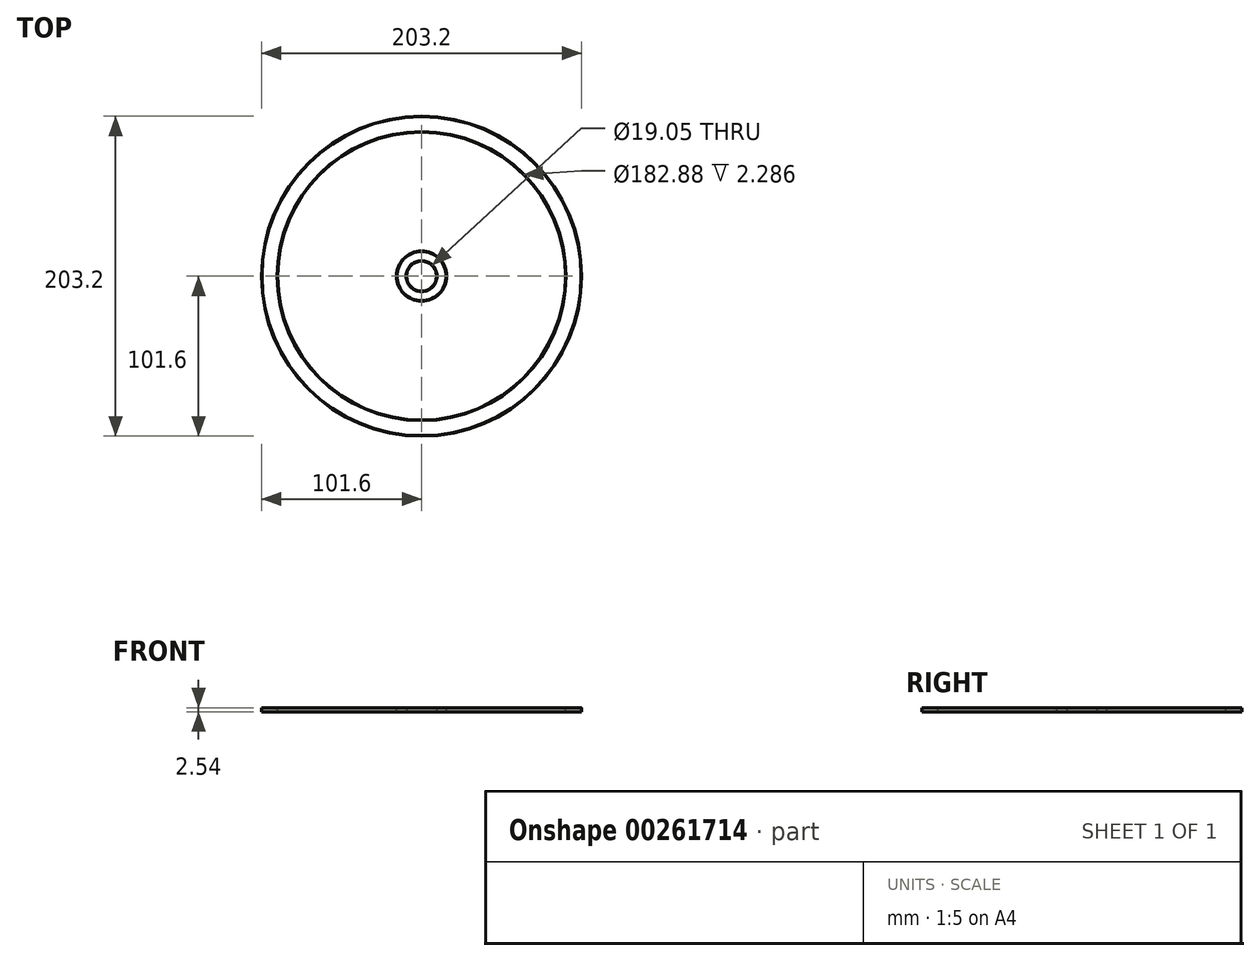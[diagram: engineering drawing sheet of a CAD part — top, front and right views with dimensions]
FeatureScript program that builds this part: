
annotation { "Feature Type Name" : "Feature", "Feature Type Description" : "" }
export const myFeature = defineFeature(function(context is Context, id is Id, definition is map)
    precondition{}
    {
        {
            var Q0;
            Q0=qCreatedBy(makeId("Top.planeOp"),FACE);
            var sketch = newSketch(context, id + "F0", { "sketchPlane" : qUnion([Q0])});
            skCircle(sketch, "E0", {"center": v(0, 0) * mm, "radius": 101.6 * mm});
            skSolve(sketch);
        }
        {
            var Q0;
            Q0=qSketchRegion(id+"F0",true);
            extrude(context, id + "F1", {"entities" : qUnion([Q0]), "depth" : 2.54 * mm});
        }
        {
            var Q0;
            Q0=makeQuery(id+"F1.opExtrude","CAP_FACE",FACE,{"disambiguationData":[OSD([sQuery(id+"F0.wireOp",EDGE,"E0")])],"isStart":true});
            var sketch = newSketch(context, id + "F2", { "sketchPlane" : qUnion([Q0])});
            skCircle(sketch, "E1", {"center": v(0, 0) * mm, "radius": 9.53 * mm});
            skSolve(sketch);
        }
        {
            var Q0;
            Q0=qSketchRegion(id+"F2",true);
            extrude(context, id + "F3", {"entities" : qUnion([Q0]), "operationType" : NewBodyOperationType.REMOVE, "oppositeDirection" : true, "depth" : 25.4 * mm});
        }
        {
            var Q0;
            Q0=makeQuery(id+"F1.opExtrude","CAP_FACE",FACE,{"disambiguationData":[OSD([sQuery(id+"F0.wireOp",EDGE,"E0")])],"isStart":false});
            var sketch = newSketch(context, id + "F4", { "sketchPlane" : qUnion([Q0])});
            skCircle(sketch, "E2", {"center": v(0, 0) * mm, "radius": 15.88 * mm});
            skCircle(sketch, "E3", {"center": v(0, 0) * mm, "radius": 91.44 * mm});
            skSolve(sketch);
        }
        {
            var Q0;
            Q0=qSketchRegion(id+"F4",true);
            extrude(context, id + "F5", {"entities" : qUnion([Q0]), "operationType" : NewBodyOperationType.REMOVE, "endBound" : BoundingType.THROUGH_ALL, "oppositeDirection" : true, "depth" : 25.4 * mm});
        }
        {
            var Q0;
            {var subQ0=sQuery(id+"F0.wireOp",EDGE,"E0");var subQ1=makeQuery(id+"F1.opExtrude","CAP_FACE",FACE,{"disambiguationData":[OSD([subQ0])],"isStart":false});Q0=makeQuery(id+"FSbwxRyUAKNEHpr_1.boolean.opBoolean","MERGE",FACE,{"derivedFrom":[makeQuery(id+"F5.boolean.opBoolean","SPLIT",FACE,{"disambiguationData":[TD([makeQuery(id+"F1.opExtrude","SWEPT_FACE",FACE,{"disambiguationData":[OSD([subQ0])]})])],"derivedFrom":subQ1}),makeQuery(id+"F5.boolean.opBoolean","SPLIT",FACE,{"disambiguationData":[TD([makeQuery(id+"F3.boolean.opBoolean","COPY",FACE,{"derivedFrom":makeQuery(id+"F3.opExtrude","SWEPT_FACE",FACE,{"disambiguationData":[OSD([sQuery(id+"F2.wireOp",EDGE,"E1")])]})})])],"derivedFrom":subQ1}),makeQuery(id+"FSbwxRyUAKNEHpr_1.opExtrude","CAP_FACE",FACE,{"disambiguationData":[OSD([sQuery(id+"FxIeaUR3CMKQrPm_1.wireOp",EDGE,"QbkZTcdc-0FBD-zTaQ-hJOD-ObugmLj84BvM"),sQuery(id+"FxIeaUR3CMKQrPm_1.wireOp",EDGE,"wRuti5NG-CyyP-u1Pt-0mSH-9gk4yfvUaacR"),sQuery(id+"FxIeaUR3CMKQrPm_1.wireOp",EDGE,"1yoEojWW-aKa5-Gd0I-27Oc-1dL5FRi6qJQZ"),sQuery(id+"FxIeaUR3CMKQrPm_1.wireOp",EDGE,"4lOamqe0-WTRM-OnQR-RPN2-e9LqBtH0SWiI"),sQuery(id+"FxIeaUR3CMKQrPm_1.wireOp",EDGE,"JicPRm3b-wYug-HpOr-Cgaa-9CY4boNc0MVj"),sQuery(id+"FxIeaUR3CMKQrPm_1.wireOp",EDGE,"sOuhCTSF-u2pH-LRFD-dapu-eMFhIlmYxAF5"),sQuery(id+"FxIeaUR3CMKQrPm_1.wireOp",EDGE,"47ca64bd-44f7-48d6-b436-1950059b13ca.1.0"),sQuery(id+"FxIeaUR3CMKQrPm_1.wireOp",EDGE,"47ca64bd-44f7-48d6-b436-1950059b13ca.1.1"),sQuery(id+"FxIeaUR3CMKQrPm_1.wireOp",EDGE,"47ca64bd-44f7-48d6-b436-1950059b13ca.1.2"),sQuery(id+"FxIeaUR3CMKQrPm_1.wireOp",EDGE,"47ca64bd-44f7-48d6-b436-1950059b13ca.1.3"),sQuery(id+"FxIeaUR3CMKQrPm_1.wireOp",EDGE,"47ca64bd-44f7-48d6-b436-1950059b13ca.2.0"),sQuery(id+"FxIeaUR3CMKQrPm_1.wireOp",EDGE,"47ca64bd-44f7-48d6-b436-1950059b13ca.2.1"),sQuery(id+"FxIeaUR3CMKQrPm_1.wireOp",EDGE,"47ca64bd-44f7-48d6-b436-1950059b13ca.2.2"),sQuery(id+"FxIeaUR3CMKQrPm_1.wireOp",EDGE,"47ca64bd-44f7-48d6-b436-1950059b13ca.2.3"),sQuery(id+"FxIeaUR3CMKQrPm_1.wireOp",EDGE,"bb024f10-06c6-412c-8647-78d520f6103a.trimOffspring"),sQuery(id+"FxIeaUR3CMKQrPm_1.wireOp",EDGE,"df42d8a4-e47c-4354-a8cb-655bc8b94241.trimOffspring"),sQuery(id+"FxIeaUR3CMKQrPm_1.wireOp",EDGE,"212b0e25-1092-4e7b-ba9c-e6eb6003562c.trimOffspring"),sQuery(id+"FxIeaUR3CMKQrPm_1.wireOp",EDGE,"8017549e-32b1-4e5e-96c6-8cc5068caf3f.trimOffspring"),sQuery(id+"FxIeaUR3CMKQrPm_1.wireOp",EDGE,"834f9041-c67c-4dd4-917f-2ef64410273a.trimOffspring"),sQuery(id+"FxIeaUR3CMKQrPm_1.wireOp",EDGE,"e2c2ff6d-6420-413b-8439-bf3ba36e34e5.trimOffspring"),sQuery(id+"FxIeaUR3CMKQrPm_1.wireOp",EDGE,"6c26bb1a-2572-49b3-b61f-98f6d5abc0ea.trimOffspring"),sQuery(id+"FxIeaUR3CMKQrPm_1.wireOp",EDGE,"b244c62b-1986-4c9c-9d84-39ec57f3331b.trimOffspring"),sQuery(id+"FxIeaUR3CMKQrPm_1.wireOp",EDGE,"19b996c0-c91f-495a-af65-c53eda865752.trimOffspring"),sQuery(id+"FxIeaUR3CMKQrPm_1.wireOp",EDGE,"542e0010-a670-4c24-a6dd-cb340de5917f.trimOffspring")])],"isStart":true})]});}
            chamfer(context, id + "F6", {"entities" : qUnion([Q0]), "width" : 0.25 * mm, "tangentPropagation" : true});
        }
    });
